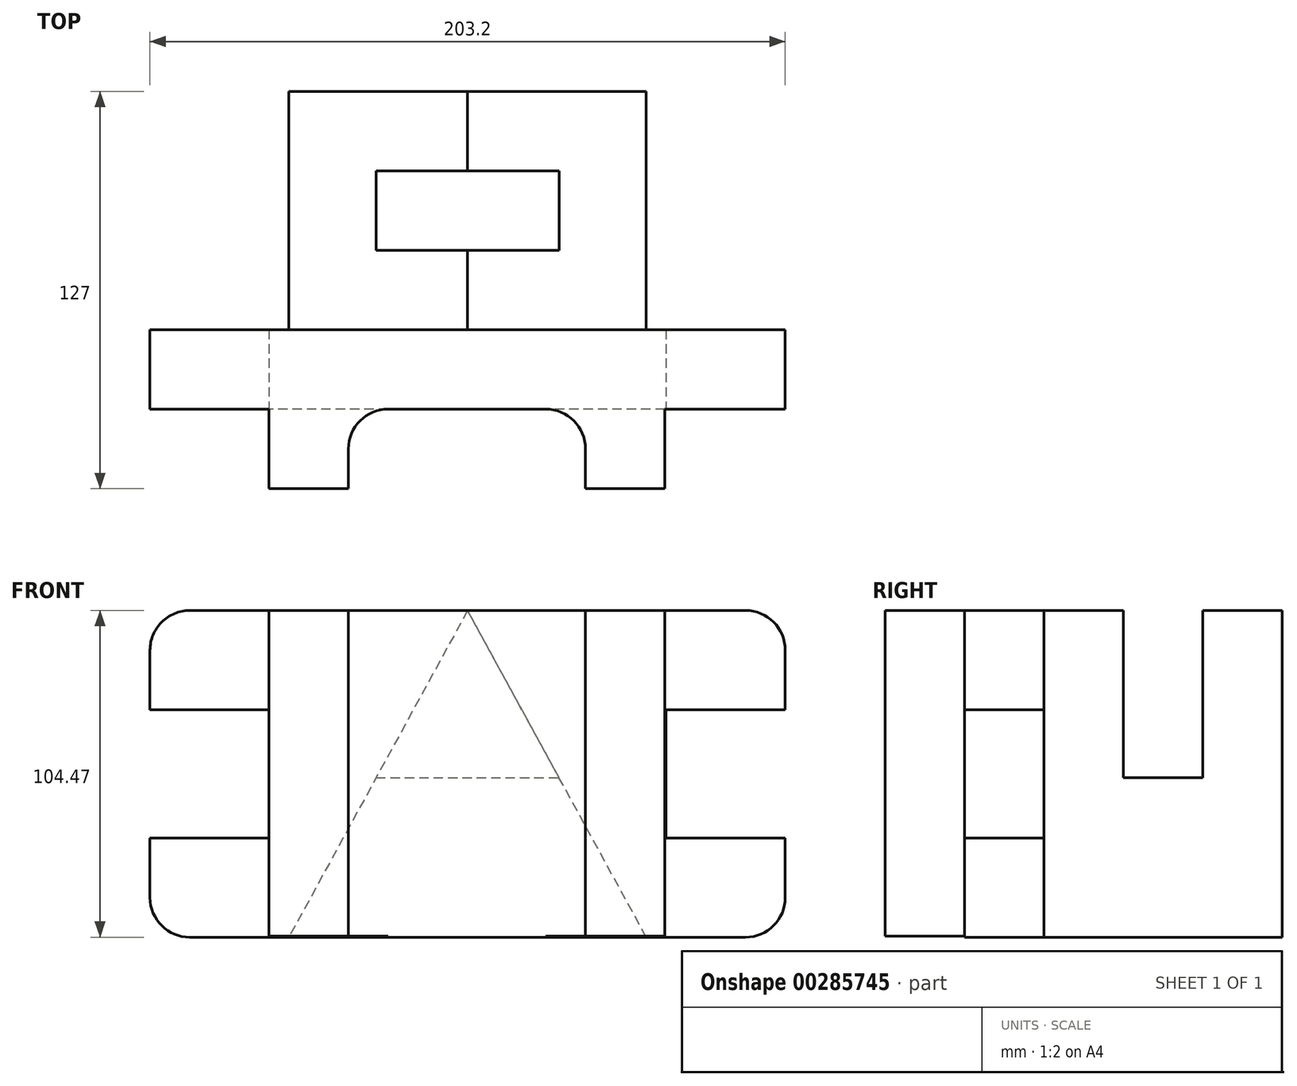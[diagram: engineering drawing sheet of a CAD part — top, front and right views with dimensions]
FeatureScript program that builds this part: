
annotation { "Feature Type Name" : "Feature", "Feature Type Description" : "" }
export const myFeature = defineFeature(function(context is Context, id is Id, definition is map)
    precondition{}
    {
        {
            var Q0;
            Q0=qCreatedBy(makeId("Front.planeOp"),FACE);
            var sketch = newSketch(context, id + "F0", { "sketchPlane" : qUnion([Q0])});
            skLineSegment(sketch, "E0", {"start": v(0, 0) * mm, "end": v(114.3, 0) * mm});
            skLineSegment(sketch, "E1", {"start": v(0, 0) * mm, "end": v(57.15, 0) * mm});
            skLineSegment(sketch, "E2", {"start": v(57.15, 0) * mm, "end": v(57.15, 53.67) * mm});
            skLineSegment(sketch, "E3", {"start": v(57.15, 53.67) * mm, "end": v(57.15, 104.47) * mm});
            skLineSegment(sketch, "E4", {"start": v(57.15, 104.47) * mm, "end": v(0, 0) * mm});
            skLineSegment(sketch, "E5", {"start": v(114.3, 0) * mm, "end": v(57.15, 104.47) * mm});
            skSolve(sketch);
        }
        {
            var Q0;
            Q0 = qSketchRegion(id + "F0", true);
            extrude(context, id + "F1", {"entities" : qUnion([Q0]), "depth" : 25.4 * mm});
        }
        {
            var Q0;
            Q0=makeQuery(id+"F1.opExtrude","CAP_FACE",FACE,{"disambiguationData":[OSD([sQuery(id+"F0.wireOp",EDGE,"E0"),sQuery(id+"F0.wireOp",EDGE,"E1"),sQuery(id+"F0.wireOp",EDGE,"E4"),sQuery(id+"F0.wireOp",EDGE,"E5")])],"isStart":false});
            var sketch = newSketch(context, id + "F2", { "sketchPlane" : qUnion([Q0])});
            skLineSegment(sketch, "E6", {"start": v(57.15, 50.96) * mm, "end": v(86.42, 50.96) * mm});
            skLineSegment(sketch, "E7", {"start": v(86.42, 50.96) * mm, "end": v(114.3, 0) * mm});
            skLineSegment(sketch, "E8", {"start": v(114.3, 0) * mm, "end": v(0, 0) * mm});
            skLineSegment(sketch, "E9", {"start": v(0, 0) * mm, "end": v(27.88, 50.96) * mm});
            skLineSegment(sketch, "E10", {"start": v(27.88, 50.96) * mm, "end": v(57.15, 50.96) * mm});
            skSolve(sketch);
        }
        {
            var Q0;
            Q0 = qSketchRegion(id + "F2", true);
            extrude(context, id + "F3", {"entities" : qUnion([Q0]), "operationType" : NewBodyOperationType.ADD, "depth" : 25.4 * mm});
        }
        {
            var Q0;
            Q0=makeQuery(id+"F3.opExtrude","CAP_FACE",FACE,{"disambiguationData":[OSD([sQuery(id+"F2.wireOp",EDGE,"E6"),sQuery(id+"F2.wireOp",EDGE,"E7"),sQuery(id+"F2.wireOp",EDGE,"E8"),sQuery(id+"F2.wireOp",EDGE,"E9"),sQuery(id+"F2.wireOp",EDGE,"E10")])],"isStart":false});
            var sketch = newSketch(context, id + "F4", { "sketchPlane" : qUnion([Q0])});
            skLineSegment(sketch, "E11", {"start": v(27.88, 50.96) * mm, "end": v(86.42, 50.96) * mm});
            skLineSegment(sketch, "E12", {"start": v(86.42, 50.96) * mm, "end": v(114.3, 0) * mm});
            skLineSegment(sketch, "E13", {"start": v(114.3, 0) * mm, "end": v(0, 0) * mm});
            skLineSegment(sketch, "E14", {"start": v(0, 0) * mm, "end": v(27.88, 50.96) * mm});
            skSolve(sketch);
        }
        {
            var Q0;
            Q0 = qSketchRegion(id + "F4", true);
            extrude(context, id + "F5", {"entities" : qUnion([Q0]), "operationType" : NewBodyOperationType.ADD, "depth" : 25.4 * mm});
        }
        {
            var Q0;
            Q0=makeQuery(id+"F5.opExtrude","CAP_FACE",FACE,{"disambiguationData":[OSD([sQuery(id+"F4.wireOp",EDGE,"E11"),sQuery(id+"F4.wireOp",EDGE,"E12"),sQuery(id+"F4.wireOp",EDGE,"E13"),sQuery(id+"F4.wireOp",EDGE,"E14")])],"isStart":false});
            var sketch = newSketch(context, id + "F6", { "sketchPlane" : qUnion([Q0])});
            skLineSegment(sketch, "E15", {"start": v(57.15, 50.96) * mm, "end": v(57.15, 104.47) * mm});
            skLineSegment(sketch, "E16", {"start": v(57.15, 104.47) * mm, "end": v(86.42, 50.96) * mm});
            skLineSegment(sketch, "E17", {"start": v(86.42, 50.96) * mm, "end": v(27.88, 50.96) * mm});
            skLineSegment(sketch, "E18", {"start": v(27.88, 50.96) * mm, "end": v(57.15, 104.47) * mm});
            skSolve(sketch);
        }
        {
            var Q0;
            Q0 = qSketchRegion(id + "F6", true);
            extrude(context, id + "F7", {"entities" : qUnion([Q0]), "operationType" : NewBodyOperationType.ADD, "oppositeDirection" : true, "depth" : 25.4 * mm});
        }
        {
            var Q0;
            Q0=makeQuery(id+"F7.boolean.opBoolean","MERGE",FACE,{"derivedFrom":[makeQuery(id+"F5.opExtrude","CAP_FACE",FACE,{"disambiguationData":[OSD([sQuery(id+"F4.wireOp",EDGE,"E11"),sQuery(id+"F4.wireOp",EDGE,"E12"),sQuery(id+"F4.wireOp",EDGE,"E13"),sQuery(id+"F4.wireOp",EDGE,"E14")])],"isStart":false}),makeQuery(id+"F7.opExtrude","CAP_FACE",FACE,{"disambiguationData":[OSD([sQuery(id+"F6.wireOp",EDGE,"E16"),sQuery(id+"F6.wireOp",EDGE,"E17"),sQuery(id+"F6.wireOp",EDGE,"E18")])],"isStart":true})]});
            var sketch = newSketch(context, id + "F8", { "sketchPlane" : qUnion([Q0])});
            skLineSegment(sketch, "E19", {"start": v(57.15, 104.47) * mm, "end": v(-6.34, 104.47) * mm});
            skLineSegment(sketch, "E20", {"start": v(-6.34, 104.47) * mm, "end": v(-6.34, 0) * mm});
            skLineSegment(sketch, "E21", {"start": v(57.15, 104.47) * mm, "end": v(120.66, 104.47) * mm});
            skLineSegment(sketch, "E22", {"start": v(120.66, 104.47) * mm, "end": v(120.66, 0) * mm});
            skLineSegment(sketch, "E23", {"start": v(120.66, 0) * mm, "end": v(-6.34, 0) * mm});
            skSolve(sketch);
        }
        {
            var Q0;
            Q0 = qSketchRegion(id + "F8", true);
            extrude(context, id + "F9", {"entities" : qUnion([Q0]), "operationType" : NewBodyOperationType.ADD, "depth" : 25.4 * mm});
        }
        {
            var Q0;
            Q0=makeQuery(id+"F9.opExtrude","CAP_FACE",FACE,{"disambiguationData":[OSD([sQuery(id+"F8.wireOp",EDGE,"E19"),sQuery(id+"F8.wireOp",EDGE,"E20"),sQuery(id+"F8.wireOp",EDGE,"E21"),sQuery(id+"F8.wireOp",EDGE,"E22"),sQuery(id+"F8.wireOp",EDGE,"E23")])],"isStart":false});
            var sketch = newSketch(context, id + "F10", { "sketchPlane" : qUnion([Q0])});
            skLineSegment(sketch, "E24", {"start": v(120.66, 104.47) * mm, "end": v(146.06, 104.47) * mm});
            skLineSegment(sketch, "E25", {"start": v(146.06, 104.47) * mm, "end": v(146.06, 72.72) * mm});
            skLineSegment(sketch, "E26", {"start": v(146.06, 72.72) * mm, "end": v(120.66, 72.72) * mm});
            skLineSegment(sketch, "E27", {"start": v(120.66, 72.72) * mm, "end": v(120.66, 104.47) * mm});
            skLineSegment(sketch, "E28", {"start": v(120.66, 0) * mm, "end": v(146.06, 0) * mm});
            skLineSegment(sketch, "E29", {"start": v(146.06, 0) * mm, "end": v(146.06, 31.75) * mm});
            skLineSegment(sketch, "E30", {"start": v(146.06, 31.75) * mm, "end": v(120.66, 31.75) * mm});
            skLineSegment(sketch, "E31", {"start": v(120.66, 31.75) * mm, "end": v(120.66, 0) * mm});
            skSolve(sketch);
        }
        {
            var Q0;
            Q0 = qSketchRegion(id + "F10", true);
            extrude(context, id + "F11", {"entities" : qUnion([Q0]), "operationType" : NewBodyOperationType.ADD, "oppositeDirection" : true, "depth" : 25.4 * mm});
        }
        {
            var Q0;
            Q0=makeQuery(id+"F11.boolean.opBoolean","MERGE",FACE,{"derivedFrom":[makeQuery(id+"F9.opExtrude","CAP_FACE",FACE,{"disambiguationData":[OSD([sQuery(id+"F8.wireOp",EDGE,"E19"),sQuery(id+"F8.wireOp",EDGE,"E20"),sQuery(id+"F8.wireOp",EDGE,"E21"),sQuery(id+"F8.wireOp",EDGE,"E22"),sQuery(id+"F8.wireOp",EDGE,"E23")])],"isStart":false}),makeQuery(id+"F11.opExtrude","CAP_FACE",FACE,{"disambiguationData":[OSD([sQuery(id+"F10.wireOp",EDGE,"E24"),sQuery(id+"F10.wireOp",EDGE,"E25"),sQuery(id+"F10.wireOp",EDGE,"E26"),sQuery(id+"F10.wireOp",EDGE,"E27")])],"isStart":true}),makeQuery(id+"F11.opExtrude","CAP_FACE",FACE,{"disambiguationData":[OSD([sQuery(id+"F10.wireOp",EDGE,"E28"),sQuery(id+"F10.wireOp",EDGE,"E29"),sQuery(id+"F10.wireOp",EDGE,"E30"),sQuery(id+"F10.wireOp",EDGE,"E31")])],"isStart":true})]});
            var sketch = newSketch(context, id + "F12", { "sketchPlane" : qUnion([Q0])});
            skLineSegment(sketch, "E32", {"start": v(-6.34, 0) * mm, "end": v(-31.74, 0) * mm});
            skLineSegment(sketch, "E33", {"start": v(-31.74, 0) * mm, "end": v(-31.74, 31.75) * mm});
            skLineSegment(sketch, "E34", {"start": v(-31.74, 31.75) * mm, "end": v(-6.34, 31.75) * mm});
            skLineSegment(sketch, "E35", {"start": v(-6.34, 31.75) * mm, "end": v(-6.34, 0) * mm});
            skLineSegment(sketch, "E36", {"start": v(-6.34, 104.47) * mm, "end": v(-31.74, 104.47) * mm});
            skLineSegment(sketch, "E37", {"start": v(-31.74, 104.47) * mm, "end": v(-31.74, 72.72) * mm});
            skLineSegment(sketch, "E38", {"start": v(-31.74, 72.72) * mm, "end": v(-6.34, 72.72) * mm});
            skLineSegment(sketch, "E39", {"start": v(-6.34, 104.47) * mm, "end": v(-6.34, 72.72) * mm});
            skSolve(sketch);
        }
        {
            var Q0;
            Q0 = qSketchRegion(id + "F12", true);
            extrude(context, id + "F13", {"entities" : qUnion([Q0]), "operationType" : NewBodyOperationType.ADD, "oppositeDirection" : true, "depth" : 25.4 * mm});
        }
        {
            var Q0;
            Q0=makeQuery(id+"F13.boolean.opBoolean","MERGE",FACE,{"derivedFrom":[makeQuery(id+"F11.boolean.opBoolean","MERGE",FACE,{"derivedFrom":[makeQuery(id+"F9.opExtrude","CAP_FACE",FACE,{"disambiguationData":[OSD([sQuery(id+"F8.wireOp",EDGE,"E19"),sQuery(id+"F8.wireOp",EDGE,"E20"),sQuery(id+"F8.wireOp",EDGE,"E21"),sQuery(id+"F8.wireOp",EDGE,"E22"),sQuery(id+"F8.wireOp",EDGE,"E23")])],"isStart":false}),makeQuery(id+"F11.opExtrude","CAP_FACE",FACE,{"disambiguationData":[OSD([sQuery(id+"F10.wireOp",EDGE,"E24"),sQuery(id+"F10.wireOp",EDGE,"E25"),sQuery(id+"F10.wireOp",EDGE,"E26"),sQuery(id+"F10.wireOp",EDGE,"E27")])],"isStart":true}),makeQuery(id+"F11.opExtrude","CAP_FACE",FACE,{"disambiguationData":[OSD([sQuery(id+"F10.wireOp",EDGE,"E28"),sQuery(id+"F10.wireOp",EDGE,"E29"),sQuery(id+"F10.wireOp",EDGE,"E30"),sQuery(id+"F10.wireOp",EDGE,"E31")])],"isStart":true})]}),makeQuery(id+"F13.opExtrude","CAP_FACE",FACE,{"disambiguationData":[OSD([sQuery(id+"F12.wireOp",EDGE,"E32"),sQuery(id+"F12.wireOp",EDGE,"E33"),sQuery(id+"F12.wireOp",EDGE,"E34"),sQuery(id+"F12.wireOp",EDGE,"E35")])],"isStart":true}),makeQuery(id+"F13.opExtrude","CAP_FACE",FACE,{"disambiguationData":[OSD([sQuery(id+"F12.wireOp",EDGE,"E36"),sQuery(id+"F12.wireOp",EDGE,"E37"),sQuery(id+"F12.wireOp",EDGE,"E38"),sQuery(id+"F12.wireOp",EDGE,"E39")])],"isStart":true})]});
            var sketch = newSketch(context, id + "F14", { "sketchPlane" : qUnion([Q0])});
            skLineSegment(sketch, "E40", {"start": v(-31.74, 31.75) * mm, "end": v(-44.44, 31.75) * mm});
            skLineSegment(sketch, "E41", {"start": v(-44.44, 31.75) * mm, "end": v(-44.44, 12.7) * mm});
            skLineSegment(sketch, "E42", {"start": v(-44.44, 12.7) * mm, "end": v(-31.74, 12.7) * mm});
            skLineSegment(sketch, "E43", {"start": v(-31.74, 12.7) * mm, "end": v(-31.74, 31.75) * mm});
            skLineSegment(sketch, "E44", {"start": v(-31.74, 72.72) * mm, "end": v(-44.44, 72.72) * mm});
            skLineSegment(sketch, "E45", {"start": v(-44.44, 72.72) * mm, "end": v(-44.44, 91.77) * mm});
            skLineSegment(sketch, "E46", {"start": v(-44.44, 91.77) * mm, "end": v(-31.74, 91.77) * mm});
            skLineSegment(sketch, "E47", {"start": v(-31.74, 91.77) * mm, "end": v(-31.74, 72.72) * mm});
            skArc(sketch, "E48", {"start": v(-31.74, 104.47) * mm, "mid": v(-40.72, 100.75) * mm, "end": v(-44.44, 91.77) * mm});
            skArc(sketch, "E49", {"start": v(-44.44, 12.7) * mm, "mid": v(-40.72, 3.72) * mm, "end": v(-31.74, 0) * mm});
            skLineSegment(sketch, "E50", {"start": v(-31.74, 104.47) * mm, "end": v(-31.74, 72.72) * mm});
            skLineSegment(sketch, "E51", {"start": v(-31.74, 31.75) * mm, "end": v(-31.74, 0) * mm});
            skSolve(sketch);
        }
        {
            var Q0;
            Q0 = qSketchRegion(id + "F14", true);
            extrude(context, id + "F15", {"entities" : qUnion([Q0]), "operationType" : NewBodyOperationType.ADD, "oppositeDirection" : true, "depth" : 25.4 * mm});
        }
        {
            var Q0;
            Q0=makeQuery(id+"F15.boolean.opBoolean","MERGE",FACE,{"derivedFrom":[makeQuery(id+"F13.boolean.opBoolean","MERGE",FACE,{"derivedFrom":[makeQuery(id+"F11.boolean.opBoolean","MERGE",FACE,{"derivedFrom":[makeQuery(id+"F9.opExtrude","CAP_FACE",FACE,{"disambiguationData":[OSD([sQuery(id+"F8.wireOp",EDGE,"E19"),sQuery(id+"F8.wireOp",EDGE,"E20"),sQuery(id+"F8.wireOp",EDGE,"E21"),sQuery(id+"F8.wireOp",EDGE,"E22"),sQuery(id+"F8.wireOp",EDGE,"E23")])],"isStart":false}),makeQuery(id+"F11.opExtrude","CAP_FACE",FACE,{"disambiguationData":[OSD([sQuery(id+"F10.wireOp",EDGE,"E24"),sQuery(id+"F10.wireOp",EDGE,"E25"),sQuery(id+"F10.wireOp",EDGE,"E26"),sQuery(id+"F10.wireOp",EDGE,"E27")])],"isStart":true}),makeQuery(id+"F11.opExtrude","CAP_FACE",FACE,{"disambiguationData":[OSD([sQuery(id+"F10.wireOp",EDGE,"E28"),sQuery(id+"F10.wireOp",EDGE,"E29"),sQuery(id+"F10.wireOp",EDGE,"E30"),sQuery(id+"F10.wireOp",EDGE,"E31")])],"isStart":true})]}),makeQuery(id+"F13.opExtrude","CAP_FACE",FACE,{"disambiguationData":[OSD([sQuery(id+"F12.wireOp",EDGE,"E32"),sQuery(id+"F12.wireOp",EDGE,"E33"),sQuery(id+"F12.wireOp",EDGE,"E34"),sQuery(id+"F12.wireOp",EDGE,"E35")])],"isStart":true}),makeQuery(id+"F13.opExtrude","CAP_FACE",FACE,{"disambiguationData":[OSD([sQuery(id+"F12.wireOp",EDGE,"E36"),sQuery(id+"F12.wireOp",EDGE,"E37"),sQuery(id+"F12.wireOp",EDGE,"E38"),sQuery(id+"F12.wireOp",EDGE,"E39")])],"isStart":true})]}),makeQuery(id+"F15.opExtrude","CAP_FACE",FACE,{"disambiguationData":[OSD([sQuery(id+"F14.wireOp",EDGE,"E40"),sQuery(id+"F14.wireOp",EDGE,"E41"),sQuery(id+"F14.wireOp",EDGE,"E49"),sQuery(id+"F14.wireOp",EDGE,"E51")])],"isStart":true}),makeQuery(id+"F15.opExtrude","CAP_FACE",FACE,{"disambiguationData":[OSD([sQuery(id+"F14.wireOp",EDGE,"E44"),sQuery(id+"F14.wireOp",EDGE,"E45"),sQuery(id+"F14.wireOp",EDGE,"E48"),sQuery(id+"F14.wireOp",EDGE,"E50")])],"isStart":true})]});
            var sketch = newSketch(context, id + "F16", { "sketchPlane" : qUnion([Q0])});
            skLineSegment(sketch, "E52", {"start": v(146.06, 72.72) * mm, "end": v(158.76, 72.72) * mm});
            skLineSegment(sketch, "E53", {"start": v(158.76, 72.72) * mm, "end": v(158.76, 91.77) * mm});
            skLineSegment(sketch, "E54", {"start": v(158.76, 91.77) * mm, "end": v(146.06, 91.77) * mm});
            skLineSegment(sketch, "E55", {"start": v(146.06, 91.77) * mm, "end": v(146.06, 72.72) * mm});
            skLineSegment(sketch, "E56", {"start": v(146.06, 31.75) * mm, "end": v(158.76, 31.75) * mm});
            skLineSegment(sketch, "E57", {"start": v(158.76, 31.75) * mm, "end": v(158.76, 12.7) * mm});
            skLineSegment(sketch, "E58", {"start": v(158.76, 12.7) * mm, "end": v(146.06, 12.7) * mm});
            skLineSegment(sketch, "E59", {"start": v(146.06, 12.7) * mm, "end": v(146.06, 31.75) * mm});
            skArc(sketch, "E60", {"start": v(158.76, 91.77) * mm, "mid": v(155.04, 100.75) * mm, "end": v(146.06, 104.47) * mm});
            skArc(sketch, "E61", {"start": v(146.06, 0) * mm, "mid": v(155.04, 3.72) * mm, "end": v(158.76, 12.7) * mm});
            skLineSegment(sketch, "E62", {"start": v(146.06, 31.75) * mm, "end": v(146.06, 0) * mm});
            skLineSegment(sketch, "E63", {"start": v(146.06, 72.72) * mm, "end": v(146.06, 104.47) * mm});
            skSolve(sketch);
        }
        {
            var Q0;
            Q0 = qSketchRegion(id + "F16", true);
            extrude(context, id + "F17", {"entities" : qUnion([Q0]), "operationType" : NewBodyOperationType.ADD, "oppositeDirection" : true, "depth" : 25.4 * mm});
        }
        {
            var Q0;
            Q0=makeQuery(id+"F13.boolean.opBoolean","MERGE",FACE,{"derivedFrom":[makeQuery(id+"F11.boolean.opBoolean","MERGE",FACE,{"derivedFrom":[makeQuery(id+"F9.opExtrude","SWEPT_FACE",FACE,{"disambiguationData":[OSD([sQuery(id+"F8.wireOp",EDGE,"E19"),sQuery(id+"F8.wireOp",EDGE,"E21")])]}),makeQuery(id+"F11.opExtrude","SWEPT_FACE",FACE,{"disambiguationData":[OSD([sQuery(id+"F10.wireOp",EDGE,"E24")])]})]}),makeQuery(id+"F13.opExtrude","SWEPT_FACE",FACE,{"disambiguationData":[OSD([sQuery(id+"F12.wireOp",EDGE,"E36")])]})]});
            var sketch = newSketch(context, id + "F18", { "sketchPlane" : qUnion([Q0])});
            skLineSegment(sketch, "E64", {"start": v(57.16, -101.6) * mm, "end": v(120.23, -101.6) * mm});
            skLineSegment(sketch, "E65", {"start": v(120.23, -101.6) * mm, "end": v(120.23, -127) * mm});
            skLineSegment(sketch, "E66", {"start": v(120.23, -127) * mm, "end": v(94.83, -127) * mm});
            skLineSegment(sketch, "E67", {"start": v(94.83, -127) * mm, "end": v(94.83, -101.6) * mm});
            skLineSegment(sketch, "E68", {"start": v(94.83, -101.6) * mm, "end": v(120.23, -101.6) * mm});
            skLineSegment(sketch, "E69", {"start": v(57.16, -101.6) * mm, "end": v(-6.36, -101.6) * mm});
            skLineSegment(sketch, "E70", {"start": v(-6.36, -101.6) * mm, "end": v(-6.36, -127) * mm});
            skLineSegment(sketch, "E71", {"start": v(-6.36, -127) * mm, "end": v(19.04, -127) * mm});
            skLineSegment(sketch, "E72", {"start": v(19.04, -127) * mm, "end": v(19.04, -101.6) * mm});
            skLineSegment(sketch, "E73", {"start": v(19.04, -101.6) * mm, "end": v(-6.36, -101.6) * mm});
            skSolve(sketch);
        }
        {
            var Q0;
            Q0 = qSketchRegion(id + "F18", true);
            extrude(context, id + "F19", {"entities" : qUnion([Q0]), "operationType" : NewBodyOperationType.ADD, "oppositeDirection" : true, "depth" : 104.14 * mm});
        }
        {
            var Q0;
            Q0=makeQuery(id+"F19.opExtrude","CAP_FACE",FACE,{"disambiguationData":[OSD([sQuery(id+"F18.wireOp",EDGE,"E70"),sQuery(id+"F18.wireOp",EDGE,"E71"),sQuery(id+"F18.wireOp",EDGE,"E72"),sQuery(id+"F18.wireOp",EDGE,"E73")])],"isStart":false});
            var sketch = newSketch(context, id + "F20", { "sketchPlane" : qUnion([Q0])});
            skLineSegment(sketch, "E74", {"start": v(19.04, 101.6) * mm, "end": v(19.04, 114.3) * mm});
            skLineSegment(sketch, "E75", {"start": v(19.04, 114.3) * mm, "end": v(19.04, 101.6) * mm});
            skLineSegment(sketch, "E76", {"start": v(19.04, 101.6) * mm, "end": v(31.74, 101.6) * mm});
            skArc(sketch, "E77", {"start": v(19.04, 114.3) * mm, "mid": v(22.75, 105.32) * mm, "end": v(31.74, 101.6) * mm});
            skSolve(sketch);
        }
        {
            var Q0;
            Q0 = qSketchRegion(id + "F20", true);
            extrude(context, id + "F21", {"entities" : qUnion([Q0]), "operationType" : NewBodyOperationType.ADD, "oppositeDirection" : true, "depth" : 104.14 * mm});
        }
        {
            var Q0;
            Q0=makeQuery(id+"F21.boolean.opBoolean","MERGE",FACE,{"derivedFrom":[makeQuery(id+"F19.boolean.opBoolean","MERGE",FACE,{"derivedFrom":[makeQuery(id+"F13.boolean.opBoolean","MERGE",FACE,{"derivedFrom":[makeQuery(id+"F11.boolean.opBoolean","MERGE",FACE,{"derivedFrom":[makeQuery(id+"F9.opExtrude","SWEPT_FACE",FACE,{"disambiguationData":[OSD([sQuery(id+"F8.wireOp",EDGE,"E19"),sQuery(id+"F8.wireOp",EDGE,"E21")])]}),makeQuery(id+"F11.opExtrude","SWEPT_FACE",FACE,{"disambiguationData":[OSD([sQuery(id+"F10.wireOp",EDGE,"E24")])]})]}),makeQuery(id+"F13.opExtrude","SWEPT_FACE",FACE,{"disambiguationData":[OSD([sQuery(id+"F12.wireOp",EDGE,"E36")])]})]}),makeQuery(id+"F19.opExtrude","CAP_FACE",FACE,{"disambiguationData":[OSD([sQuery(id+"F18.wireOp",EDGE,"E65"),sQuery(id+"F18.wireOp",EDGE,"E66"),sQuery(id+"F18.wireOp",EDGE,"E67"),sQuery(id+"F18.wireOp",EDGE,"E68")])],"isStart":true}),makeQuery(id+"F19.opExtrude","CAP_FACE",FACE,{"disambiguationData":[OSD([sQuery(id+"F18.wireOp",EDGE,"E70"),sQuery(id+"F18.wireOp",EDGE,"E71"),sQuery(id+"F18.wireOp",EDGE,"E72"),sQuery(id+"F18.wireOp",EDGE,"E73")])],"isStart":true})]}),makeQuery(id+"F21.opExtrude","CAP_FACE",FACE,{"disambiguationData":[OSD([sQuery(id+"F20.wireOp",EDGE,"E76"),sQuery(id+"F20.wireOp",EDGE,"E77"),sQuery(id+"F20.wireOp",EDGE,"E75")])],"isStart":false})]});
            var sketch = newSketch(context, id + "F22", { "sketchPlane" : qUnion([Q0])});
            skLineSegment(sketch, "E78", {"start": v(94.83, -101.6) * mm, "end": v(82.13, -101.6) * mm});
            skLineSegment(sketch, "E79", {"start": v(94.83, -101.6) * mm, "end": v(94.83, -114.3) * mm});
            skArc(sketch, "E80", {"start": v(94.83, -114.3) * mm, "mid": v(91.11, -105.32) * mm, "end": v(82.13, -101.6) * mm});
            skLineSegment(sketch, "E81", {"start": v(94.83, -114.3) * mm, "end": v(94.83, -101.6) * mm});
            skSolve(sketch);
        }
        {
            var Q0;
            Q0 = qSketchRegion(id + "F22", true);
            extrude(context, id + "F23", {"entities" : qUnion([Q0]), "operationType" : NewBodyOperationType.ADD, "oppositeDirection" : true, "depth" : 104.14 * mm});
        }
    });
